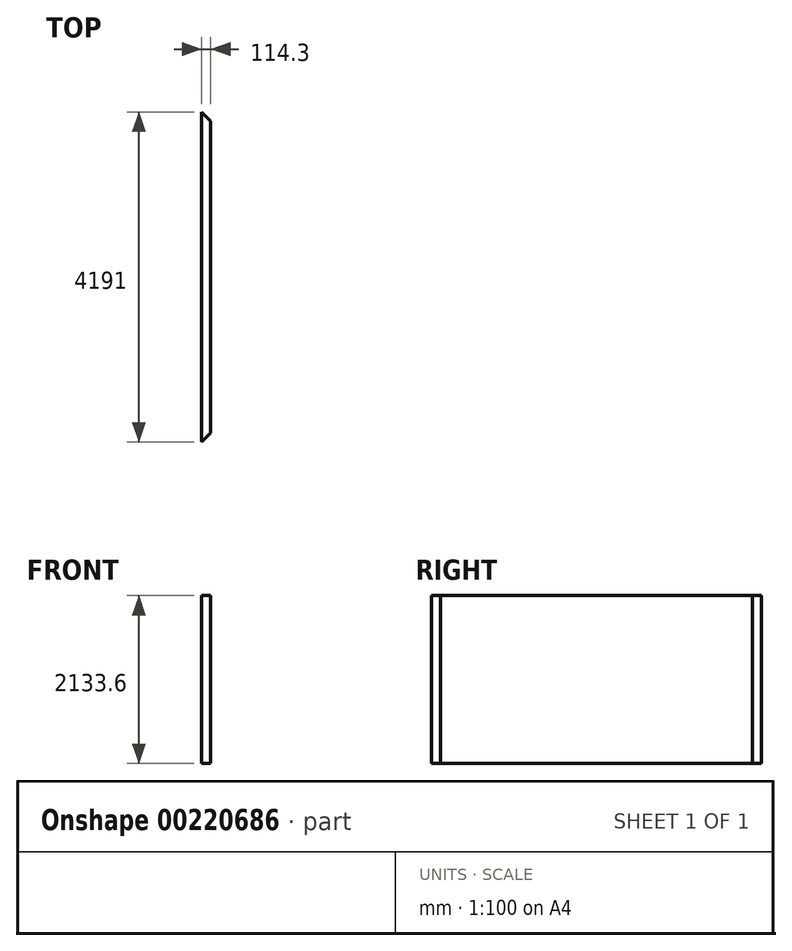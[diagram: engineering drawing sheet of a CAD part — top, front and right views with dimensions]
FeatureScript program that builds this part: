
annotation { "Feature Type Name" : "Feature", "Feature Type Description" : "" }
export const myFeature = defineFeature(function(context is Context, id is Id, definition is map)
    precondition{}
    {
        {
            var Q0;
            Q0=qCreatedBy(makeId("Top.planeOp"),FACE);
            var sketch = newSketch(context, id + "F0", { "sketchPlane" : qUnion([Q0])});
            skLineSegment(sketch, "E0.bottom", {"start": v(1993.9, -57.15) * mm, "end": v(-1993.9, -57.15) * mm});
            skLineSegment(sketch, "E0.top", {"start": v(1993.9, 57.15) * mm, "end": v(-1993.9, 57.15) * mm});
            skLineSegment(sketch, "E0.left", {"start": v(1993.9, -57.15) * mm, "end": v(1993.9, 57.15) * mm});
            skLineSegment(sketch, "E0.right", {"start": v(-1993.9, -57.15) * mm, "end": v(-1993.9, 57.15) * mm});
            skPoint(sketch, "E0.middle", {"position": v(0, 0) * mm});
            skLineSegment(sketch, "E1", {"start": v(-1993.9, 57.15) * mm, "end": v(-2108.2, 57.15) * mm});
            skLineSegment(sketch, "E2", {"start": v(-2108.2, 57.15) * mm, "end": v(-1993.9, -57.15) * mm});
            skLineSegment(sketch, "E3", {"start": v(1993.9, 57.15) * mm, "end": v(2108.2, 57.15) * mm});
            skLineSegment(sketch, "E4", {"start": v(2108.2, 57.15) * mm, "end": v(1993.9, -57.15) * mm});
            skSolve(sketch);
        }
        {
            var Q0;
            Q0=makeQuery(id+"F0.imprint","IMPRINT",FACE,{"disambiguationData":[TD([[makeQuery(id+"F0.imprint","IMPRINT",EDGE,{"derivedFrom":sQuery(id+"F0.wireOp",EDGE,"E0.right")}),1.0]])]});
            var Q1;
            Q1=makeQuery(id+"F0.imprint","IMPRINT",FACE,{"disambiguationData":[TD([[makeQuery(id+"F0.imprint","IMPRINT",EDGE,{"derivedFrom":sQuery(id+"F0.wireOp",EDGE,"E0.bottom")}),-1.0]])]});
            var Q2;
            Q2=makeQuery(id+"F0.imprint","IMPRINT",FACE,{"disambiguationData":[TD([[makeQuery(id+"F0.imprint","IMPRINT",EDGE,{"derivedFrom":sQuery(id+"F0.wireOp",EDGE,"E0.left")}),-1.0]])]});
            extrude(context, id + "F1", {"entities" : qUnion([Q0, Q1, Q2]), "endBound" : BoundingType.SYMMETRIC, "depth" : 2133.6 * mm});
        }
        {
            var Q0;
            Q0=makeQuery(id+"F1.opExtrude","SWEPT_BODY",BODY,{"disambiguationData":[OSD([sQuery(id+"F0.wireOp",EDGE,"E0.bottom"),sQuery(id+"F0.wireOp",EDGE,"E0.top"),sQuery(id+"F0.wireOp",EDGE,"E1"),sQuery(id+"F0.wireOp",EDGE,"E2"),sQuery(id+"F0.wireOp",EDGE,"E3"),sQuery(id+"F0.wireOp",EDGE,"E4")])]});
            deleteBodies(context, id + "F2", {"entities" : qUnion([Q0])});
        }
        {
            var Q0;
            Q0=qCreatedBy(makeId("Top.planeOp"),FACE);
            var sketch = newSketch(context, id + "F3", { "sketchPlane" : qUnion([Q0])});
            skLineSegment(sketch, "E5.bottom", {"start": v(57.15, -1981.2) * mm, "end": v(-57.15, -1981.2) * mm});
            skLineSegment(sketch, "E5.top", {"start": v(57.15, 1981.2) * mm, "end": v(-57.15, 1981.2) * mm});
            skLineSegment(sketch, "E5.left", {"start": v(57.15, -1981.2) * mm, "end": v(57.15, 1981.2) * mm});
            skLineSegment(sketch, "E5.right", {"start": v(-57.15, -1981.2) * mm, "end": v(-57.15, 1981.2) * mm});
            skPoint(sketch, "E5.middle", {"position": v(0, 0) * mm});
            skLineSegment(sketch, "E6", {"start": v(-57.15, -1981.2) * mm, "end": v(-57.15, -2002.25) * mm});
            skLineSegment(sketch, "E7", {"start": v(-57.15, -1981.2) * mm, "end": v(-57.15, -2095.5) * mm});
            skLineSegment(sketch, "E8", {"start": v(-57.15, -2095.5) * mm, "end": v(57.15, -1981.2) * mm});
            skLineSegment(sketch, "E9", {"start": v(-57.15, 1981.2) * mm, "end": v(-57.15, 2002.33) * mm});
            skLineSegment(sketch, "E10", {"start": v(-57.15, 1981.2) * mm, "end": v(-57.15, 2095.5) * mm});
            skLineSegment(sketch, "E11", {"start": v(-57.15, 2095.5) * mm, "end": v(57.15, 1981.2) * mm});
            skSolve(sketch);
        }
        {
            var Q0;
            {var subQ0=sQuery(id+"F3.wireOp",EDGE,"E5.bottom");Q0=makeQuery(id+"F3.imprint","IMPRINT",FACE,{"disambiguationData":[TD([[makeQuery(id+"F3.imprint","IMPRINT",EDGE,{"derivedFrom":subQ0}),1.0]])]});}
            var Q1;
            Q1=makeQuery(id+"F3.imprint","IMPRINT",FACE,{"disambiguationData":[TD([[makeQuery(id+"F3.imprint","IMPRINT",EDGE,{"derivedFrom":sQuery(id+"F3.wireOp",EDGE,"E5.bottom")}),-1.0]])]});
            var Q2;
            {var subQ0=sQuery(id+"F3.wireOp",EDGE,"E5.top");Q2=makeQuery(id+"F3.imprint","IMPRINT",FACE,{"disambiguationData":[TD([[makeQuery(id+"F3.imprint","IMPRINT",EDGE,{"derivedFrom":subQ0}),-1.0]])]});}
            extrude(context, id + "F4", {"entities" : qUnion([Q0, Q1, Q2]), "endBound" : BoundingType.SYMMETRIC, "depth" : 2133.6 * mm});
        }
    });
